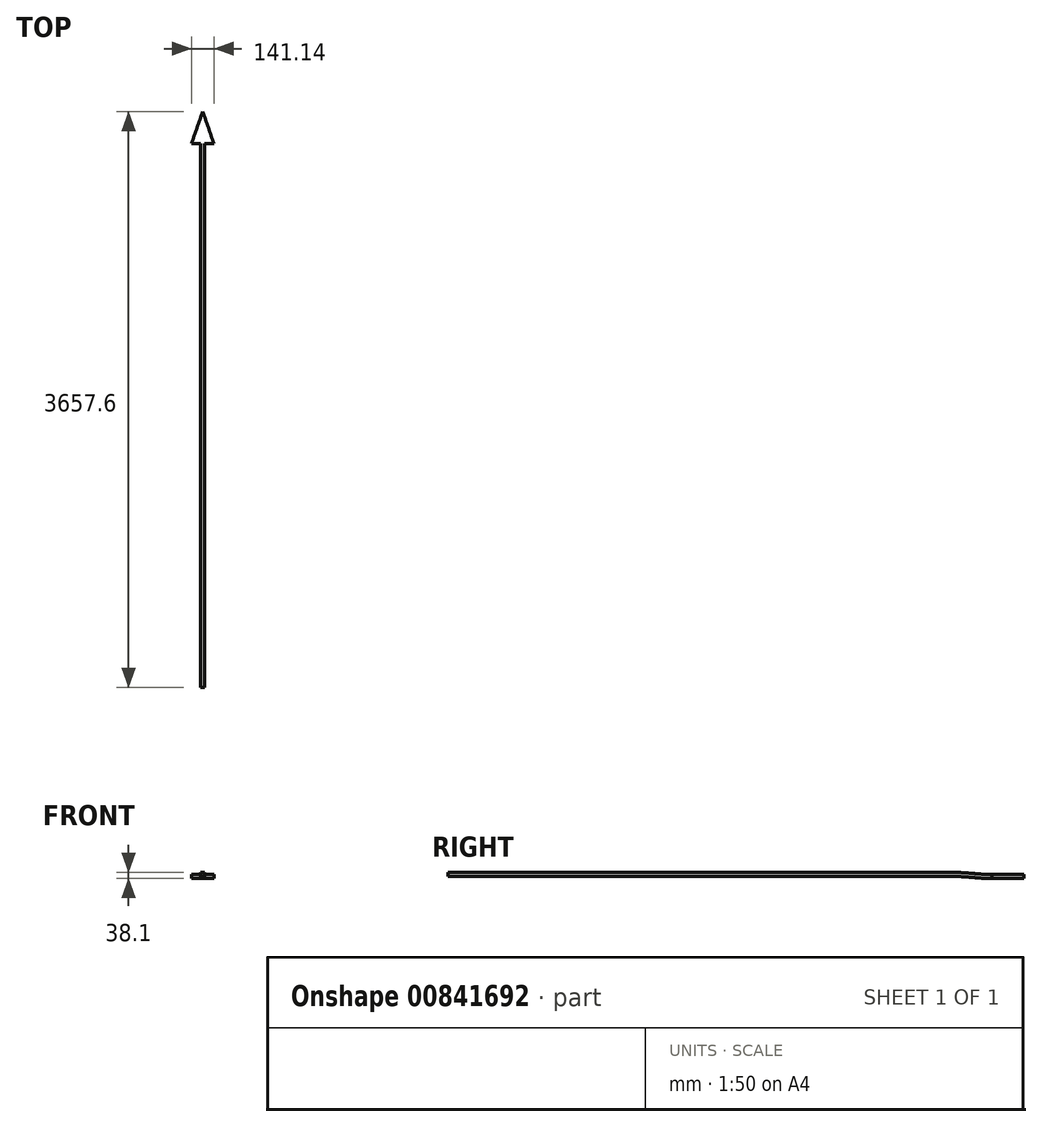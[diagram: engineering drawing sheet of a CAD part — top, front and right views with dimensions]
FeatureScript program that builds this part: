
annotation { "Feature Type Name" : "Feature", "Feature Type Description" : "" }
export const myFeature = defineFeature(function(context is Context, id is Id, definition is map)
    precondition{}
    {
        {
            var Q0;
            Q0=qCreatedBy(makeId("Top.planeOp"),FACE);
            var sketch = newSketch(context, id + "F0", { "sketchPlane" : qUnion([Q0])});
            skLineSegment(sketch, "E0", {"start": v(0, -1828.8) * mm, "end": v(0, 1828.8) * mm, "construction": true});
            skLineSegment(sketch, "E1", {"start": v(0, -1828.8) * mm, "end": v(-228.6, -1828.8) * mm, "construction": true});
            skLineSegment(sketch, "E2", {"start": v(0, 0) * mm, "end": v(-381, 0) * mm, "construction": true});
            skArc(sketch, "E3", {"start": v(0, 1828.8) * mm, "mid": v(-6.38, 1811.3) * mm, "end": v(-12.7, 1793.8) * mm});
            skLineSegment(sketch, "E4", {"start": v(0, -1828.8) * mm, "end": v(-12.7, -1828.8) * mm});
            skLineSegment(sketch, "E5", {"start": v(-12.7, -1828.8) * mm, "end": v(-12.7, 1793.8) * mm});
            skLineSegment(sketch, "E6.MirrorCS", {"start": v(12.7, -1828.8) * mm, "end": v(12.7, 1793.8) * mm});
            skLineSegment(sketch, "E7", {"start": v(0, -1828.8) * mm, "end": v(12.7, -1828.8) * mm});
            skArc(sketch, "E8.trimOffspring", {"start": v(-381, 0) * mm, "mid": v(-370.28, -919.86) * mm, "end": v(-228.6, -1828.8) * mm});
            skArc(sketch, "E9.MirrorCS", {"start": v(0, 1828.8) * mm, "mid": v(6.38, 1811.3) * mm, "end": v(12.7, 1793.8) * mm});
            skSolve(sketch);
        }
        {
            var Q0;
            Q0=makeQuery(id+"F0.imprint","IMPRINT",FACE,{"disambiguationData":[TD([[makeQuery(id+"F0.imprint","IMPRINT",EDGE,{"derivedFrom":sQuery(id+"F0.wireOp",EDGE,"E4")}),-1.0]])]});
            extrude(context, id + "F1", {"entities" : qUnion([Q0]), "depth" : 38.1 * mm, "offsetDistance" : 25.4 * mm});
        }
        {
            var Q0;
            Q0=makeQuery(id+"F1.opExtrude","SWEPT_FACE",FACE,{"disambiguationData":[OSD([sQuery(id+"F0.wireOp",EDGE,"E6.MirrorCS")])]});
            var sketch = newSketch(context, id + "F2", { "sketchPlane" : qUnion([Q0])});
            skLineSegment(sketch, "E10", {"start": v(-1828.8, 0) * mm, "end": v(-1828.8, 12.7) * mm});
            skLineSegment(sketch, "E11", {"start": v(-1828.8, 12.7) * mm, "end": v(1371.6, 12.7) * mm});
            skLineSegment(sketch, "E12", {"start": v(1625.6, 0) * mm, "end": v(1828.8, 0) * mm, "construction": true});
            skLineSegment(sketch, "E13", {"start": v(1828.8, 0) * mm, "end": v(1828.8, 25.4) * mm, "construction": true});
            skArc(sketch, "E14", {"start": v(1498.6, 6.35) * mm, "mid": v(1435.18, 11.11) * mm, "end": v(1371.6, 12.7) * mm});
            skArc(sketch, "E15", {"start": v(1498.6, 6.35) * mm, "mid": v(1562.02, 1.59) * mm, "end": v(1625.6, 0) * mm});
            skLineSegment(sketch, "E16", {"start": v(-1828.8, 0) * mm, "end": v(1625.6, 0) * mm});
            skLineSegment(sketch, "E17", {"start": v(1828.8, 25.4) * mm, "end": v(1828.8, 38.1) * mm});
            skLineSegment(sketch, "E18", {"start": v(1828.8, 38.1) * mm, "end": v(1371.6, 38.1) * mm});
            skLineSegment(sketch, "E19", {"start": v(1371.6, 38.1) * mm, "end": v(1371.6, 12.7) * mm, "construction": true});
            skLineSegment(sketch, "E20", {"start": v(1828.8, 25.4) * mm, "end": v(1625.6, 25.4) * mm});
            skLineSegment(sketch, "E21", {"start": v(1625.6, 25.4) * mm, "end": v(1625.6, 0) * mm, "construction": true});
            skArc(sketch, "E22", {"start": v(1498.6, 31.75) * mm, "mid": v(1435.18, 36.51) * mm, "end": v(1371.6, 38.1) * mm});
            skArc(sketch, "E23", {"start": v(1498.6, 31.75) * mm, "mid": v(1562.02, 26.99) * mm, "end": v(1625.6, 25.4) * mm});
            skSolve(sketch);
        }
        {
            var Q0;
            Q0 = qSketchRegion(id + "F2", true);
            extrude(context, id + "F3", {"entities" : qUnion([Q0]), "operationType" : NewBodyOperationType.REMOVE, "oppositeDirection" : true, "depth" : 25.4 * mm, "offsetDistance" : 25.4 * mm});
        }
        {
            var Q0;
            Q0=makeQuery(id+"F3.boolean.opBoolean","COPY",FACE,{"derivedFrom":makeQuery(id+"F3.opExtrude","SWEPT_FACE",FACE,{"disambiguationData":[OSD([sQuery(id+"F2.wireOp",EDGE,"E20")])]})});
            var sketch = newSketch(context, id + "F4", { "sketchPlane" : qUnion([Q0])});
            skLineSegment(sketch, "E24", {"start": v(0, 0) * mm, "end": v(-381, 0) * mm, "construction": true});
            skLineSegment(sketch, "E25", {"start": v(0, -1828.8) * mm, "end": v(-228.6, -1828.8) * mm, "construction": true});
            skLineSegment(sketch, "E26", {"start": v(0, 1828.8) * mm, "end": v(0, 1625.6) * mm, "construction": true});
            skLineSegment(sketch, "E27", {"start": v(-12.7, 1625.6) * mm, "end": v(-70.57, 1625.6) * mm});
            skArc(sketch, "E28", {"start": v(-12.7, 1793.8) * mm, "mid": v(-42.21, 1709.9) * mm, "end": v(-70.57, 1625.6) * mm});
            skLineSegment(sketch, "E29", {"start": v(-12.7, 1625.6) * mm, "end": v(-12.7, 1793.8) * mm});
            skArc(sketch, "E30.trimOffspring", {"start": v(-381, 0) * mm, "mid": v(-370.28, -919.86) * mm, "end": v(-228.6, -1828.8) * mm, "construction": true});
            skLineSegment(sketch, "E31.MirrorCS", {"start": v(12.7, 1625.6) * mm, "end": v(12.7, 1793.8) * mm});
            skArc(sketch, "E32.MirrorCS", {"start": v(12.7, 1793.8) * mm, "mid": v(42.21, 1709.9) * mm, "end": v(70.57, 1625.6) * mm});
            skLineSegment(sketch, "E33.MirrorCS", {"start": v(12.7, 1625.6) * mm, "end": v(70.57, 1625.6) * mm});
            skSolve(sketch);
        }
        {
            var Q0;
            Q0 = qSketchRegion(id + "F4", true);
            extrude(context, id + "F5", {"entities" : qUnion([Q0]), "operationType" : NewBodyOperationType.ADD, "oppositeDirection" : true, "depth" : 25.4 * mm, "offsetDistance" : 25.4 * mm});
        }
    });
